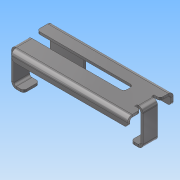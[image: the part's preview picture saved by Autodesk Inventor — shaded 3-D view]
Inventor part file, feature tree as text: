
AUTODESK INVENTOR PART (.ipt)
format: ipt  version: 2016 (Build 200138000, 138)  size: 285,696 bytes
history: native  units: mm
features: sheet_metal_op x15, sketch x8, other x8, projected_geometry x2, chamfer x1
ambient origin geometry x8: Origin, YZ Plane, XZ Plane, XY Plane, X Axis, Y Axis, Z Axis, Center Point
bodies: Body1 (feature_tree)
feature tree (34):
  sheet_metal_op  "Contour Flange1"
  sheet_metal_op  "Flange1"
  sheet_metal_op  "Flange2"
  sheet_metal_op  "Flange3"
  sheet_metal_op  "Flange4"
  chamfer  "Corner Round1"
  sketch  "Sketch10"  dims[d7=3.0mm]
  other  "Plate1"
  sheet_metal_op  "Bend1"
  sheet_metal_op  "Corner1"
  sketch  "Sketch11"  dims[d8=3.8mm]
  other  "Plate2"
  sheet_metal_op  "Bend2"
  sheet_metal_op  "Corner2"
  sketch  "Sketch12"  dims[d9=0.76mm]
  other  "Plate3"
  sheet_metal_op  "Bend3"
  sheet_metal_op  "Corner3"
  sketch  "Sketch13"  dims[d10=0.9mm]
  projected_geometry  "Projected Loop1"
  sketch  "Sketch14"  dims[d11=0.2mm]
  other  "Plate4"
  sheet_metal_op  "Bend4"
  sheet_metal_op  "Corner4"
  sketch  "Sketch15"  dims[d12=0.1mm]
  other  "Plate5"
  sheet_metal_op  "Bend5"
  sheet_metal_op  "Corner5"
  sketch  "Sketch16"  dims[d13=0.4mm]
  sketch  "Sketch17"  dims[d14=0.2mm d15=10.0mm d16=0.2mm d17=0.5mm d18=0.8mm d19=0.2mm d20=0.2mm d21=0.2mm d22=0.1mm d23=0.4mm d24=0.2mm d25=3.0mm d26=90.0deg d27=0.2mm d28=1.2mm d29=0.8mm d30=0.2mm d31=0.2mm d32=0.2mm d33=0.1mm d34=0.4mm d35=0.2mm d36=1.0mm d37=90.0deg d38=0.2mm d39=0.8mm d40=0.2mm d41=0.2mm d42=1.3mm d43=0.8mm d44=8.0mm d45=0.2mm d46=0.0mm d47=0.2mm d48=0.1mm d49=0.4mm d50=0.2mm d51=3.0mm d52=90.0deg d53=0.2mm d54=0.8mm d55=0.2mm d56=0.2mm d58=0.2mm d59=0.1mm d60=0.4mm d61=0.2mm d62=1.0mm d63=90.0deg d64=0.2mm d65=0.8mm d66=0.2mm d67=0.2mm d68=2.75mm d69=1.0mm d70=0.8mm d71=0.2mm d72=0.0mm d73=0.2mm d74=0.0mm d75=0.25mm]
  projected_geometry  "Projected Loop2"
  other  "Cut1"
  other  "Cut2"
  other  "Cut3"
